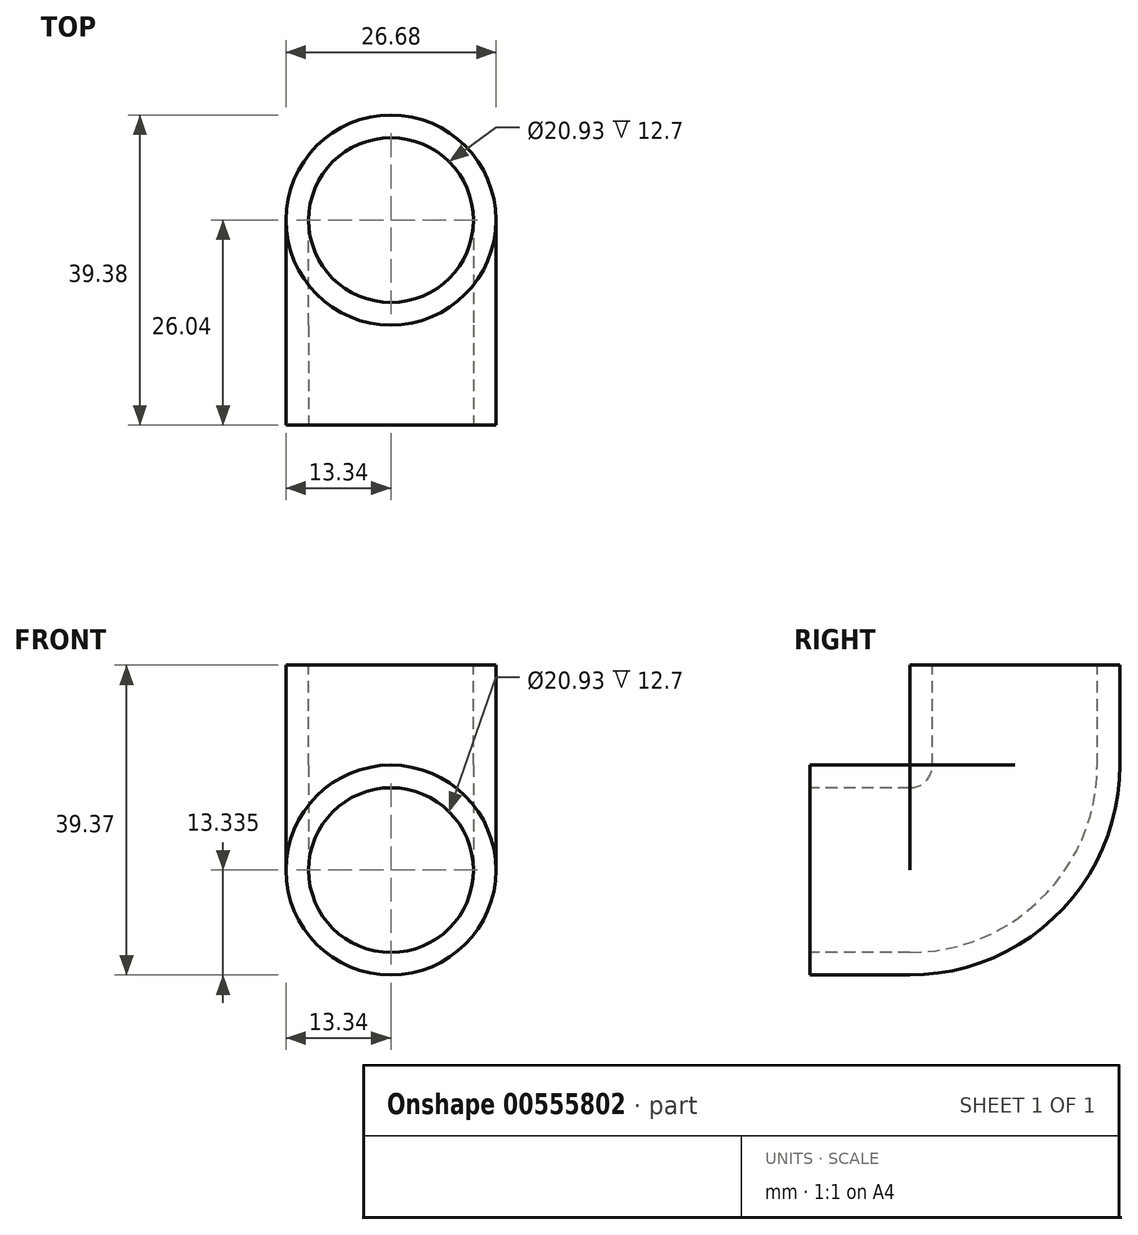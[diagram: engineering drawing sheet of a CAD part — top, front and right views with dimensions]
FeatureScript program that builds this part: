
annotation { "Feature Type Name" : "Feature", "Feature Type Description" : "" }
export const myFeature = defineFeature(function(context is Context, id is Id, definition is map)
    precondition{}
    {
        {
            var Q0;
            Q0=qCreatedBy(makeId("Top.planeOp"),FACE);
            var sketch = newSketch(context, id + "F0", { "sketchPlane" : qUnion([Q0])});
            skCircle(sketch, "E0", {"center": v(0, 0) * mm, "radius": 13.33 * mm});
            skCircle(sketch, "E1", {"center": v(0, 0) * mm, "radius": 10.46 * mm});
            skSolve(sketch);
        }
        {
            var Q0;
            Q0=qCreatedBy(makeId("Right.planeOp"),FACE);
            var sketch = newSketch(context, id + "F1", { "sketchPlane" : qUnion([Q0])});
            skArc(sketch, "E2", {"start": v(-13.34, -13.33) * mm, "mid": v(-3.9, -9.43) * mm, "end": v(0, 0) * mm});
            skSolve(sketch);
        }
        {
            var Q0;
            Q0=makeQuery(id+"F0.imprint","IMPRINT",FACE,{"disambiguationData":[TD([[makeQuery(id+"F0.imprint","IMPRINT",EDGE,{"derivedFrom":sQuery(id+"F0.wireOp",EDGE,"E0")}),1.0]])]});
            var Q1;
            Q1=sQuery(id+"F1.wireOp",EDGE,"E2");
            sweep(context, id + "F2", {"profiles" : qUnion([Q0]), "path" : qUnion([Q1])});
        }
        {
            var Q0;
            Q0=qCreatedBy(makeId("Right.planeOp"),FACE);
            var sketch = newSketch(context, id + "F3", { "sketchPlane" : qUnion([Q0])});
            skLineSegment(sketch, "E3", {"start": v(0, 0) * mm, "end": v(0, 12.7) * mm});
            skSolve(sketch);
        }
        {
            var Q0;
            Q0=makeQuery(id+"F2.opSweep","CAP_FACE",FACE,{"disambiguationData":[OSD([sQuery(id+"F0.wireOp",EDGE,"E0"),sQuery(id+"F0.wireOp",EDGE,"E1"),sQuery(id+"F1.wireOp",VERTEX,"E2.end")])],"isStart":true});
            var Q1;
            Q1=sQuery(id+"F3.wireOp",EDGE,"E3");
            sweep(context, id + "F4", {"operationType" : NewBodyOperationType.ADD, "profiles" : qUnion([Q0]), "path" : qUnion([Q1])});
        }
        {
            var Q0;
            Q0=qCreatedBy(makeId("Right.planeOp"),FACE);
            var sketch = newSketch(context, id + "F5", { "sketchPlane" : qUnion([Q0])});
            skLineSegment(sketch, "E4", {"start": v(-42.86, -73.02) * mm, "end": v(-55.56, -73.02) * mm});
            skLineSegment(sketch, "E5", {"start": v(-55.56, -73.02) * mm, "end": v(-42.86, -73.02) * mm});
            skSolve(sketch);
        }
        {
            var Q0;
            Q0=makeQuery(id+"F2.opSweep","CAP_FACE",FACE,{"disambiguationData":[OSD([sQuery(id+"F0.wireOp",EDGE,"E0"),sQuery(id+"F0.wireOp",EDGE,"E1"),sQuery(id+"F1.wireOp",VERTEX,"E2.start")])],"isStart":false});
            var Q1;
            Q1=sQuery(id+"F5.wireOp",EDGE,"E4");
            sweep(context, id + "F6", {"operationType" : NewBodyOperationType.ADD, "profiles" : qUnion([Q0]), "path" : qUnion([Q1])});
        }
    });
